# Revit family: Gira_125027
name_source: partatom
category: Electrical Fixtures
revit_build: Autodesk Revit 2017 (Build: 20160225_1515(x64)
units: mm (PartAtom-declared; Revit-internal decimal feet)

## family parameters
Cut with Voids When Loaded = No
Host = Face
Maintain Annotation Orientation = No
Part Type = Normal
Room Calculation Point = No
Round Connector Dimension = Use Diameter
Shared = No

## types (1)
- SM home st. System 55 p.white m
    Add-on device = No
    Automatic door opener = Yes
    Available = No
    BIM (1) = https://media.stage.bim.site
    Can be connected to smartphone = No
    Category = Indoor station door communication
    Colour = White
    Control extra function(s) = Yes
    Data sheet (1) = https://katalog.gira.de
    Default Elevation = 1219 mm
    Description = SM home st. Sys55 PWm,Surface-mounted home station,System 55,pure white matt,Features:,- Completely pre-assembled surface-mounted home station This facilitates fast and clean installation.,- Design diversity thanks to integration into the design line, allowing uniform appearance of door communication and electrical installation.,- Installation possible with or without frame.,- Easy installation with plug-in screw terminals on the mounting plate. Contact to the home station is established when the home station is attached to the mounting plate.,- Easy disassembly of the home station during renovation work.,- Mounting holes for installation.,- Signal transmission and power supply of home station via reverse-polarity-protected and short-circuit-proof 2-wire bus.,- Parallel connection of up to three home stations is possible (with power supply via the 2-wire bus).,- One-man start-up with easy start-up procedure.,- Ringtone differentiation for door call, internal call and floor call.,- Choice of five different ringtone melodies for separate assignment to specific call buttons.,- Speakerphone function (voice-controlled talk-back with echo and background noise suppression).,- Enforcement function for loud background noises during the voice connection.,- Eavesdropping prevention.,- Operating buttons with integrated LEDs for status display.,The operating buttons of the surface-mounted home station control the following functions in connection with the switching actuator or the flush-mounted switching actuator::,- Switching of lights and other functions.,- Control of the door opener.,- Setting the ringtone melody.,- Switching the ringtone on and off.,- Call acceptance.,- Activation of the enforcement function.,- Adjustment of ring tone and voice volume.,,Notes :,- Installation without frame is possible.,- A 2-gang cover frame without crossbar is required for installation with System 55 or the Gira F100 and Gira E22 design lines.,- A frame is required for installation in a device box,- This component enables door communication systems with up to 70 devices to be set up,  (e.g. 1 x built-in speaker, 5 x add-on modules for built-in speakers, 68 x surface-mounted home stations).
    Function lamps = Yes
    GTIN = 4010337010470
    HAN = 125001
    Hearing aid compatible = No
    HeinzeBIM = https://bimportal.heinze.de
    Installation technique = Bus system
    Internal communication = Yes
    Loudness control = Yes
    Manufacturer = Gira
    Manufacturer URL = https://www.gira.de
    Material = Other
    Mounting method = Surface mounted (plaster)
    Mutable call tone = Yes
    Name = SM home st. System 55 cr.white
    Operation door lock = Yes
    Overhear protected = Yes
    Specific call tone = Yes
    URL = http://katalog.gira.de
    With memory function = No
    With touch screen = No
    With video = No

## geometry (parser evidence)
native form markers: Sweep x2
no freeform markers — native parametric forms only
